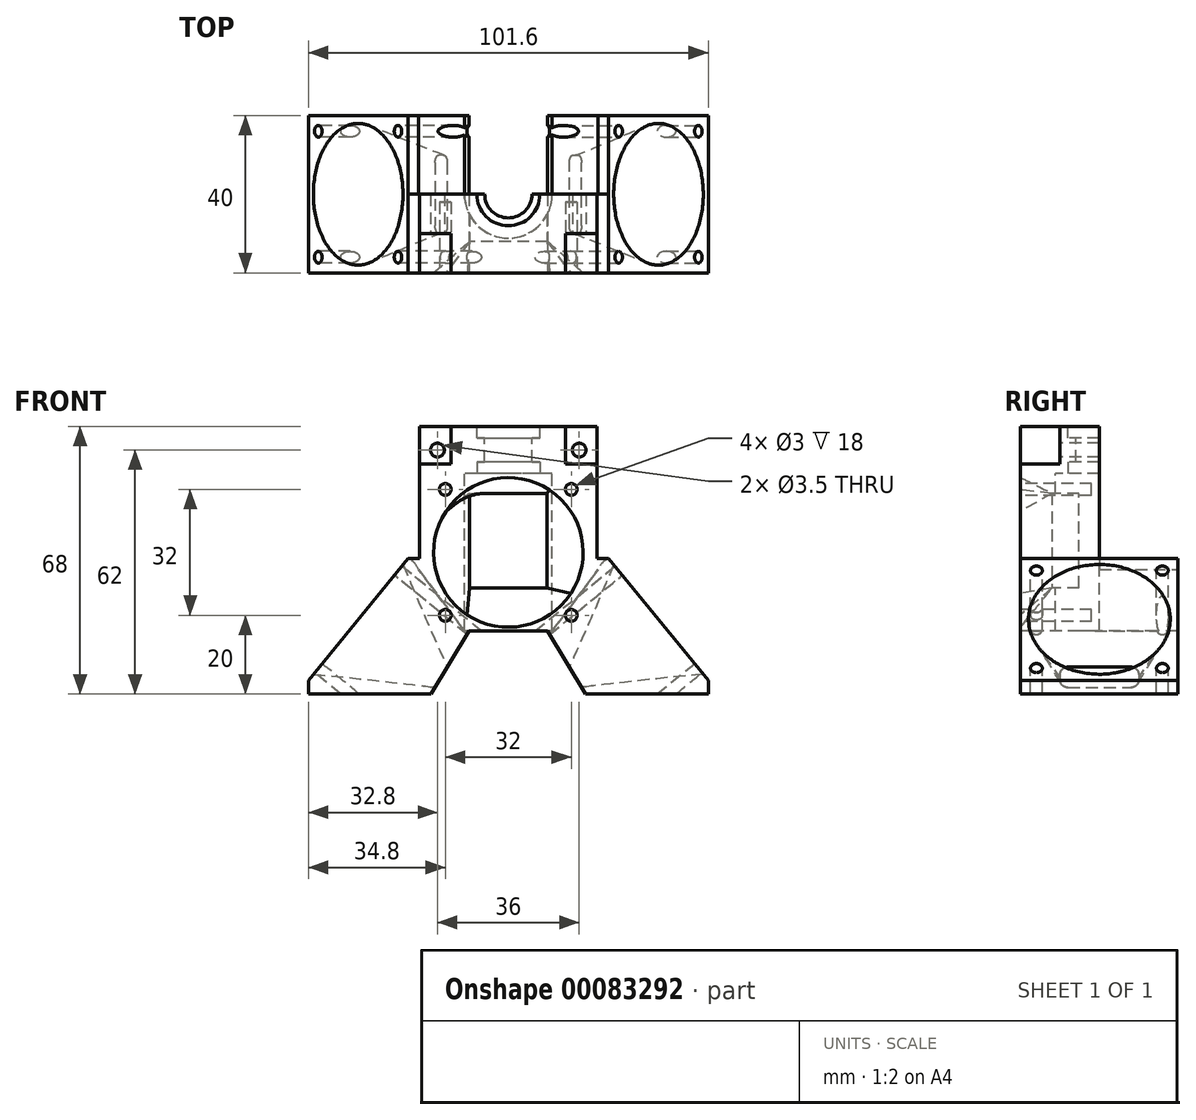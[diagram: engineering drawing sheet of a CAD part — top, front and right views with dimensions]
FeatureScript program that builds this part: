
annotation { "Feature Type Name" : "Feature", "Feature Type Description" : "" }
export const myFeature = defineFeature(function(context is Context, id is Id, definition is map)
    precondition{}
    {
        {
            var Q0;
            Q0=qCreatedBy(makeId("Front.planeOp"),FACE);
            var sketch = newSketch(context, id + "F0", { "sketchPlane" : qUnion([Q0])});
            skLineSegment(sketch, "E0.bottom", {"start": v(22.5, 6) * mm, "end": v(-22.5, 6) * mm});
            skLineSegment(sketch, "E0.top", {"start": v(22.5, -6) * mm, "end": v(-22.5, -6) * mm});
            skLineSegment(sketch, "E0.left", {"start": v(22.5, 6) * mm, "end": v(22.5, -6) * mm});
            skLineSegment(sketch, "E0.right", {"start": v(-22.5, 6) * mm, "end": v(-22.5, -6) * mm});
            skPoint(sketch, "E0.middle", {"position": v(0, 0) * mm});
            skCircle(sketch, "E1", {"center": v(-18, 0) * mm, "radius": 1.75 * mm});
            skCircle(sketch, "E2", {"center": v(-18, 0) * mm, "radius": 3.5 * mm, "construction": true});
            skCircle(sketch, "E3", {"center": v(18, 0) * mm, "radius": 1.75 * mm});
            skCircle(sketch, "E4", {"center": v(18, 0) * mm, "radius": 3.5 * mm, "construction": true});
            skLineSegment(sketch, "E5.bottom", {"start": v(-22.5, 6) * mm, "end": v(-14.5, 6) * mm});
            skLineSegment(sketch, "E5.top", {"start": v(-22.5, -3.5) * mm, "end": v(-14.5, -3.5) * mm});
            skLineSegment(sketch, "E5.left", {"start": v(-22.5, 6) * mm, "end": v(-22.5, -3.5) * mm});
            skLineSegment(sketch, "E5.right", {"start": v(-14.5, 6) * mm, "end": v(-14.5, -3.5) * mm});
            skLineSegment(sketch, "E6.bottom", {"start": v(22.5, 6) * mm, "end": v(14.5, 6) * mm});
            skLineSegment(sketch, "E6.top", {"start": v(22.5, -3.5) * mm, "end": v(14.5, -3.5) * mm});
            skLineSegment(sketch, "E6.left", {"start": v(22.5, 6) * mm, "end": v(22.5, -3.5) * mm});
            skLineSegment(sketch, "E6.right", {"start": v(14.5, 6) * mm, "end": v(14.5, -3.5) * mm});
            skSolve(sketch);
        }
        {
            var Q0;
            Q0=qSketchRegion(id+"F0",true);
            var Q1;
            Q1=makeQuery(id+"F0.imprint","IMPRINT",FACE,{"disambiguationData":[TD([[makeQuery(id+"F0.imprint","IMPRINT",EDGE,{"derivedFrom":sQuery(id+"F0.wireOp",EDGE,"E1")}),-1.0]])]});
            var Q2;
            Q2=makeQuery(id+"F0.imprint","IMPRINT",FACE,{"disambiguationData":[TD([[makeQuery(id+"F0.imprint","IMPRINT",EDGE,{"derivedFrom":sQuery(id+"F0.wireOp",EDGE,"E3")}),-1.0]])]});
            extrude(context, id + "F1", {"entities" : qUnion([Q0, Q1, Q2]), "oppositeDirection" : true, "depth" : 20 * mm});
        }
        {
            var Q0;
            Q0=makeQuery(id+"F0.imprint","IMPRINT",FACE,{"disambiguationData":[TD([[makeQuery(id+"F0.imprint","IMPRINT",EDGE,{"derivedFrom":sQuery(id+"F0.wireOp",EDGE,"E1")}),-1.0]])]});
            var Q1;
            Q1=makeQuery(id+"F0.imprint","IMPRINT",FACE,{"disambiguationData":[TD([[makeQuery(id+"F0.imprint","IMPRINT",EDGE,{"derivedFrom":sQuery(id+"F0.wireOp",EDGE,"E3")}),-1.0]])]});
            extrude(context, id + "F2", {"entities" : qUnion([Q0, Q1]), "operationType" : NewBodyOperationType.REMOVE, "oppositeDirection" : true, "depth" : 10 * mm});
        }
        {
            var Q0;
            Q0=makeQuery(id+"F1.opExtrude","SWEPT_FACE",FACE,{"disambiguationData":[OSD([sQuery(id+"F0.wireOp",EDGE,"E0.bottom")])]});
            var sketch = newSketch(context, id + "F3", { "sketchPlane" : qUnion([Q0])});
            skCircle(sketch, "E7", {"center": v(0, 20) * mm, "radius": 6 * mm});
            skCircle(sketch, "E8", {"center": v(0, 20) * mm, "radius": 8 * mm});
            skSolve(sketch);
        }
        {
            var Q0;
            {var subQ0=sQuery(id+"F3.wireOp",EDGE,"E7");var subQ1=makeQuery(id+"F1.opExtrude","CAP_EDGE",EDGE,{"disambiguationData":[OSD([sQuery(id+"F0.wireOp",EDGE,"E0.bottom")])],"isStart":false});var subQ2=makeQuery(id+"F3.imprint","INTERSECT",VERTEX,{"disambiguationData":[OD(0.0)],"derivedFrom":[subQ1,subQ0]});Q0=makeQuery(id+"F3.imprint","IMPRINT",FACE,{"disambiguationData":[TD([[makeQuery(id+"F3.imprint","IMPRINT",EDGE,{"disambiguationData":[TD([[subQ2,-1.0]])],"derivedFrom":subQ0}),1.0]])]});}
            var Q1;
            {var subQ0=sQuery(id+"F3.wireOp",EDGE,"E7");var subQ1=makeQuery(id+"F1.opExtrude","CAP_EDGE",EDGE,{"disambiguationData":[OSD([sQuery(id+"F0.wireOp",EDGE,"E0.bottom")])],"isStart":false});var subQ2=makeQuery(id+"F3.imprint","INTERSECT",VERTEX,{"disambiguationData":[OD(0.0)],"derivedFrom":[subQ1,subQ0]});Q1=makeQuery(id+"F3.imprint","IMPRINT",FACE,{"disambiguationData":[TD([[makeQuery(id+"F3.imprint","IMPRINT",EDGE,{"disambiguationData":[TD([[subQ2,1.0]])],"derivedFrom":subQ0}),1.0]])]});}
            extrude(context, id + "F4", {"entities" : qUnion([Q0, Q1]), "operationType" : NewBodyOperationType.REMOVE, "endBound" : BoundingType.THROUGH_ALL, "oppositeDirection" : true, "depth" : 25 * mm});
        }
        {
            var Q0;
            Q0=qSketchRegion(id+"F3",true);
            extrude(context, id + "F5", {"entities" : qUnion([Q0]), "operationType" : NewBodyOperationType.REMOVE, "oppositeDirection" : true, "depth" : 3 * mm});
        }
        {
            var Q0;
            Q0=makeQuery(id+"F1.opExtrude","SWEPT_FACE",FACE,{"disambiguationData":[OSD([sQuery(id+"F0.wireOp",EDGE,"E0.top")])]});
            var sketch = newSketch(context, id + "F6", { "sketchPlane" : qUnion([Q0])});
            skCircle(sketch, "E9", {"center": v(0, -20) * mm, "radius": 8 * mm});
            skSolve(sketch);
        }
        {
            var Q0;
            Q0=qSketchRegion(id+"F6",true);
            extrude(context, id + "F7", {"entities" : qUnion([Q0]), "operationType" : NewBodyOperationType.REMOVE, "oppositeDirection" : true, "depth" : 3 * mm});
        }
        {
            var Q0;
            {var subQ0=sQuery(id+"F0.wireOp",EDGE,"E0.top");Q0=makeQuery(id+"F6.imprint","IMPRINT",FACE,{"disambiguationData":[TD([[makeQuery(id+"F6.imprint","IMPRINT",EDGE,{"derivedFrom":makeQuery(id+"F1.opExtrude","CAP_EDGE",EDGE,{"disambiguationData":[OSD([subQ0])],"isStart":true})}),1.0]])]});}
            var sketch = newSketch(context, id + "F8", { "sketchPlane" : qUnion([Q0])});
            skLineSegment(sketch, "E10.bottom", {"start": v(-22.5, 0) * mm, "end": v(22.5, 0) * mm});
            skLineSegment(sketch, "E10.top", {"start": v(-22.5, -20) * mm, "end": v(-11.15, -20) * mm});
            skLineSegment(sketch, "E10.left", {"start": v(-22.5, 0) * mm, "end": v(-22.5, -20) * mm});
            skLineSegment(sketch, "E10.right", {"start": v(22.5, 0) * mm, "end": v(22.5, -20) * mm});
            skArc(sketch, "E11", {"start": v(11.15, -20) * mm, "mid": v(0, -8.85) * mm, "end": v(-11.15, -20) * mm});
            skLineSegment(sketch, "E12.trimOffspring", {"start": v(11.15, -20) * mm, "end": v(22.5, -20) * mm});
            skSolve(sketch);
        }
        {
            var Q0;
            Q0=qSketchRegion(id+"F8",true);
            extrude(context, id + "F9", {"entities" : qUnion([Q0]), "operationType" : NewBodyOperationType.ADD, "depth" : 40 * mm});
        }
        {
            var Q0;
            Q0=makeQuery(id+"F9.boolean.opBoolean","MERGE",FACE,{"derivedFrom":[makeQuery(id+"F1.opExtrude","CAP_FACE",FACE,{"disambiguationData":[OSD([sQuery(id+"F0.wireOp",EDGE,"E0.bottom"),sQuery(id+"F0.wireOp",EDGE,"E0.top"),sQuery(id+"F0.wireOp",EDGE,"E0.left"),sQuery(id+"F0.wireOp",EDGE,"E0.right"),sQuery(id+"F0.wireOp",EDGE,"E1"),sQuery(id+"F0.wireOp",EDGE,"E3")])],"isStart":true}),makeQuery(id+"F9.opExtrude","SWEPT_FACE",FACE,{"disambiguationData":[OSD([sQuery(id+"F8.wireOp",EDGE,"E10.bottom")])]})]});
            cPlane(context, id + "F10", {"entities" : qUnion([Q0]), "cplaneType" : CPlaneType.OFFSET, "offset" : 8 * mm, "oppositeDirection" : true, "width" : 150 * mm, "height" : 150 * mm});
        }
        {
            var Q0;
            Q0=qCreatedBy(id+"F10.planeOp",FACE);
            var sketch = newSketch(context, id + "F11", { "sketchPlane" : qUnion([Q0])});
            skLineSegment(sketch, "E13.bottom", {"start": v(9.89, -11) * mm, "end": v(-9.89, -11) * mm});
            skLineSegment(sketch, "E13.top", {"start": v(9.89, -35) * mm, "end": v(-9.89, -35) * mm});
            skLineSegment(sketch, "E13.left", {"start": v(9.89, -11) * mm, "end": v(9.89, -35) * mm});
            skLineSegment(sketch, "E13.right", {"start": v(-9.89, -11) * mm, "end": v(-9.89, -35) * mm});
            skPoint(sketch, "E13.middle", {"position": v(0, -23) * mm});
            skSolve(sketch);
        }
        {
            var Q0;
            Q0=makeQuery(id+"F9.boolean.opBoolean","MERGE",FACE,{"derivedFrom":[makeQuery(id+"F1.opExtrude","CAP_FACE",FACE,{"disambiguationData":[OSD([sQuery(id+"F0.wireOp",EDGE,"E0.bottom"),sQuery(id+"F0.wireOp",EDGE,"E0.top"),sQuery(id+"F0.wireOp",EDGE,"E0.left"),sQuery(id+"F0.wireOp",EDGE,"E0.right"),sQuery(id+"F0.wireOp",EDGE,"E1"),sQuery(id+"F0.wireOp",EDGE,"E3")])],"isStart":true}),makeQuery(id+"F9.opExtrude","SWEPT_FACE",FACE,{"disambiguationData":[OSD([sQuery(id+"F8.wireOp",EDGE,"E10.bottom")])]})]});
            var sketch = newSketch(context, id + "F12", { "sketchPlane" : qUnion([Q0])});
            skCircle(sketch, "E14", {"center": v(0, -26) * mm, "radius": 19 * mm});
            skSolve(sketch);
        }
        {
            var Q1;
            Q1=qSketchRegion(id+"F11",true);
            var Q2;
            Q2=qSketchRegion(id+"F12",true);
            loft(context, id + "F13", {"operationType" : NewBodyOperationType.REMOVE, "sheetProfilesArray" : [{ "sheetProfileEntities" : qUnion([Q1]) }, { "sheetProfileEntities" : qUnion([Q2]) }]});
        }
        {
            var Q0;
            Q0=qSketchRegion(id+"F11",true);
            extrude(context, id + "F14", {"entities" : qUnion([Q0]), "operationType" : NewBodyOperationType.REMOVE, "endBound" : BoundingType.THROUGH_ALL, "oppositeDirection" : true, "depth" : 25 * mm});
        }
        {
            var Q0;
            Q0=makeQuery(id+"F9.boolean.opBoolean","MERGE",FACE,{"derivedFrom":[makeQuery(id+"F1.opExtrude","CAP_FACE",FACE,{"disambiguationData":[OSD([sQuery(id+"F0.wireOp",EDGE,"E0.bottom"),sQuery(id+"F0.wireOp",EDGE,"E0.top"),sQuery(id+"F0.wireOp",EDGE,"E0.left"),sQuery(id+"F0.wireOp",EDGE,"E0.right"),sQuery(id+"F0.wireOp",EDGE,"E1"),sQuery(id+"F0.wireOp",EDGE,"E3")])],"isStart":true}),makeQuery(id+"F9.opExtrude","SWEPT_FACE",FACE,{"disambiguationData":[OSD([sQuery(id+"F8.wireOp",EDGE,"E10.bottom")])]})]});
            var sketch = newSketch(context, id + "F15", { "sketchPlane" : qUnion([Q0])});
            skLineSegment(sketch, "E15.bottom", {"start": v(16, -10) * mm, "end": v(-16, -10) * mm, "construction": true});
            skLineSegment(sketch, "E15.top", {"start": v(16, -42) * mm, "end": v(-16, -42) * mm, "construction": true});
            skLineSegment(sketch, "E15.left", {"start": v(16, -10) * mm, "end": v(16, -42) * mm, "construction": true});
            skLineSegment(sketch, "E15.right", {"start": v(-16, -10) * mm, "end": v(-16, -42) * mm, "construction": true});
            skPoint(sketch, "E15.middle", {"position": v(0, -26) * mm});
            skCircle(sketch, "E16", {"center": v(16, -10) * mm, "radius": 1.5 * mm});
            skCircle(sketch, "E17", {"center": v(-16, -10) * mm, "radius": 1.5 * mm});
            skCircle(sketch, "E18", {"center": v(-16, -42) * mm, "radius": 1.5 * mm});
            skCircle(sketch, "E19", {"center": v(16, -42) * mm, "radius": 1.5 * mm});
            skSolve(sketch);
        }
        {
            var Q0;
            Q0=qSketchRegion(id+"F15",true);
            extrude(context, id + "F16", {"entities" : qUnion([Q0]), "operationType" : NewBodyOperationType.REMOVE, "oppositeDirection" : true, "depth" : 18 * mm});
        }
        {
            var Q0;
            Q0=qCreatedBy(makeId("Front.planeOp"),FACE);
            var sketch = newSketch(context, id + "F17", { "sketchPlane" : qUnion([Q0])});
            skPoint(sketch, "E20", {"position": v(0, -68) * mm});
            skLineSegment(sketch, "E21", {"start": v(0, -68) * mm, "end": v(-20, -55.95) * mm, "construction": true});
            skLineSegment(sketch, "E22", {"start": v(-50.8, -58.5) * mm, "end": v(-50.8, -62) * mm});
            skLineSegment(sketch, "E23", {"start": v(-50.8, -62) * mm, "end": v(-19.64, -62) * mm});
            skLineSegment(sketch, "E24", {"start": v(-19.64, -62) * mm, "end": v(-10, -46) * mm});
            skLineSegment(sketch, "E25", {"start": v(-22.5, -27.52) * mm, "end": v(-25.5, -27.52) * mm});
            skLineSegment(sketch, "E26", {"start": v(-25.5, -27.52) * mm, "end": v(-50.8, -58.5) * mm});
            skPoint(sketch, "E27", {"position": v(-10, -61.97) * mm});
            skLineSegment(sketch, "E28", {"start": v(-22.5, -46) * mm, "end": v(-22.5, -27.52) * mm});
            skLineSegment(sketch, "E29", {"start": v(-10, -46) * mm, "end": v(-22.5, -46) * mm});
            skLineSegment(sketch, "E30", {"start": v(0, 42.58) * mm, "end": v(0, -74.7) * mm, "construction": true});
            skLineSegment(sketch, "E31.MirrorCS", {"start": v(50.8, -58.5) * mm, "end": v(50.8, -62) * mm});
            skLineSegment(sketch, "E32.MirrorCS", {"start": v(22.5, -27.52) * mm, "end": v(25.5, -27.52) * mm});
            skLineSegment(sketch, "E33.MirrorCS", {"start": v(0, -68) * mm, "end": v(20, -55.95) * mm, "construction": true});
            skLineSegment(sketch, "E34.MirrorCS", {"start": v(19.64, -62) * mm, "end": v(10, -46) * mm});
            skPoint(sketch, "E35.MirrorP", {"position": v(10, -61.97) * mm});
            skLineSegment(sketch, "E36.MirrorCS", {"start": v(50.8, -62) * mm, "end": v(19.64, -62) * mm});
            skLineSegment(sketch, "E37.MirrorCS", {"start": v(10, -46) * mm, "end": v(22.5, -46) * mm});
            skLineSegment(sketch, "E38.MirrorCS", {"start": v(22.5, -46) * mm, "end": v(22.5, -27.52) * mm});
            skLineSegment(sketch, "E39.MirrorCS", {"start": v(25.5, -27.52) * mm, "end": v(50.8, -58.5) * mm});
            skSolve(sketch);
        }
        {
            var Q0;
            Q0=makeQuery(id+"F17.imprint","IMPRINT",FACE,{"disambiguationData":[TD([[makeQuery(id+"F17.imprint","IMPRINT",EDGE,{"derivedFrom":sQuery(id+"F17.wireOp",EDGE,"f7ET7okq-i3aG-xWv0-ujYL-7c9q7adUJRvd")}),1.0]])]});
            var Q1;
            Q1=makeQuery(id+"F17.imprint","IMPRINT",FACE,{"disambiguationData":[TD([[makeQuery(id+"F17.imprint","IMPRINT",EDGE,{"derivedFrom":sQuery(id+"F17.wireOp",EDGE,"E22")}),1.0]])]});
            var Q2;
            Q2=makeQuery(id+"F17.imprint","IMPRINT",FACE,{"disambiguationData":[TD([[makeQuery(id+"F17.imprint","IMPRINT",EDGE,{"derivedFrom":sQuery(id+"F17.wireOp",EDGE,"E31.MirrorCS")}),-1.0]])]});
            extrude(context, id + "F18", {"entities" : qUnion([Q0, Q1, Q2]), "operationType" : NewBodyOperationType.ADD, "oppositeDirection" : true, "depth" : 40 * mm});
        }
        {
            var Q0;
            Q0=makeQuery(id+"F18.opExtrude","SWEPT_FACE",FACE,{"disambiguationData":[OSD([sQuery(id+"F17.wireOp",EDGE,"E26")])]});
            var sketch = newSketch(context, id + "F19", { "sketchPlane" : qUnion([Q0])});
            skCircle(sketch, "E40", {"center": v(-20, -57.45) * mm, "radius": 18 * mm});
            skSolve(sketch);
        }
        {
            var Q0;
            Q0=makeQuery(id+"F18.opExtrude","SWEPT_FACE",FACE,{"disambiguationData":[OSD([sQuery(id+"F17.wireOp",EDGE,"E24")])]});
            var sketch = newSketch(context, id + "F20", { "sketchPlane" : qUnion([Q0])});
            skLineSegment(sketch, "E41.bottom", {"start": v(28, -55.24) * mm, "end": v(12, -55.24) * mm});
            skLineSegment(sketch, "E41.top", {"start": v(28, -61.24) * mm, "end": v(12, -61.24) * mm});
            skLineSegment(sketch, "E41.left", {"start": v(30, -57.24) * mm, "end": v(30, -59.24) * mm});
            skLineSegment(sketch, "E41.right", {"start": v(10, -57.24) * mm, "end": v(10, -59.24) * mm});
            skPoint(sketch, "E41.middle", {"position": v(20, -58.24) * mm});
            skPoint(sketch, "E42.visualSharp", {"position": v(10, -55.24) * mm});
            skArc(sketch, "E42.filletArc", {"start": v(12, -55.24) * mm, "mid": v(10.59, -55.83) * mm, "end": v(10, -57.24) * mm});
            skPoint(sketch, "E43.visualSharp", {"position": v(10, -61.24) * mm});
            skArc(sketch, "E43.filletArc", {"start": v(10, -59.24) * mm, "mid": v(10.59, -60.66) * mm, "end": v(12, -61.24) * mm});
            skPoint(sketch, "E44.visualSharp", {"position": v(30, -61.24) * mm});
            skArc(sketch, "E44.filletArc", {"start": v(28, -61.24) * mm, "mid": v(29.41, -60.66) * mm, "end": v(30, -59.24) * mm});
            skPoint(sketch, "E45.visualSharp", {"position": v(30, -55.24) * mm});
            skArc(sketch, "E45.filletArc", {"start": v(30, -57.24) * mm, "mid": v(29.41, -55.83) * mm, "end": v(28, -55.24) * mm});
            skSolve(sketch);
        }
        {
            var Q1;
            Q1=makeQuery(id+"F19.imprint","IMPRINT",FACE,{"disambiguationData":[TD([[makeQuery(id+"F19.imprint","IMPRINT",EDGE,{"derivedFrom":sQuery(id+"F19.wireOp",EDGE,"E40")}),1.0]])]});
            var Q2;
            Q2=makeQuery(id+"F20.imprint","IMPRINT",FACE,{"disambiguationData":[TD([[makeQuery(id+"F20.imprint","IMPRINT",EDGE,{"derivedFrom":sQuery(id+"F20.wireOp",EDGE,"E41.bottom")}),1.0]])]});
            loft(context, id + "F21", {"operationType" : NewBodyOperationType.REMOVE, "sheetProfilesArray" : [{ "sheetProfileEntities" : qUnion([Q1]) }, { "sheetProfileEntities" : qUnion([Q2]) }]});
        }
        {
            var Q0;
            Q0=makeQuery(id+"F18.opExtrude","SWEPT_FACE",FACE,{"disambiguationData":[OSD([sQuery(id+"F17.wireOp",EDGE,"E39.MirrorCS")])]});
            var sketch = newSketch(context, id + "F22", { "sketchPlane" : qUnion([Q0])});
            skCircle(sketch, "E46", {"center": v(20, -57.45) * mm, "radius": 18 * mm});
            skSolve(sketch);
        }
        {
            var Q0;
            Q0=makeQuery(id+"F18.opExtrude","SWEPT_FACE",FACE,{"disambiguationData":[OSD([sQuery(id+"F17.wireOp",EDGE,"E34.MirrorCS")])]});
            var sketch = newSketch(context, id + "F23", { "sketchPlane" : qUnion([Q0])});
            skLineSegment(sketch, "E47.bottom", {"start": v(-12, -55.24) * mm, "end": v(-28, -55.24) * mm});
            skLineSegment(sketch, "E47.top", {"start": v(-12, -61.24) * mm, "end": v(-28, -61.24) * mm});
            skLineSegment(sketch, "E47.left", {"start": v(-10, -57.24) * mm, "end": v(-10, -59.24) * mm});
            skLineSegment(sketch, "E47.right", {"start": v(-30, -57.24) * mm, "end": v(-30, -59.24) * mm});
            skPoint(sketch, "E47.middle", {"position": v(-20, -58.24) * mm});
            skPoint(sketch, "E48.visualSharp", {"position": v(-30, -55.24) * mm});
            skArc(sketch, "E48.filletArc", {"start": v(-28, -55.24) * mm, "mid": v(-29.41, -55.83) * mm, "end": v(-30, -57.24) * mm});
            skPoint(sketch, "E49.visualSharp", {"position": v(-10, -55.24) * mm});
            skArc(sketch, "E49.filletArc", {"start": v(-10, -57.24) * mm, "mid": v(-10.59, -55.83) * mm, "end": v(-12, -55.24) * mm});
            skPoint(sketch, "E50.visualSharp", {"position": v(-10, -61.24) * mm});
            skArc(sketch, "E50.filletArc", {"start": v(-12, -61.24) * mm, "mid": v(-10.59, -60.66) * mm, "end": v(-10, -59.24) * mm});
            skPoint(sketch, "E51.visualSharp", {"position": v(-30, -61.24) * mm});
            skArc(sketch, "E51.filletArc", {"start": v(-30, -59.24) * mm, "mid": v(-29.41, -60.66) * mm, "end": v(-28, -61.24) * mm});
            skSolve(sketch);
        }
        {
            var Q1;
            Q1=makeQuery(id+"F22.imprint","IMPRINT",FACE,{"disambiguationData":[TD([[makeQuery(id+"F22.imprint","IMPRINT",EDGE,{"derivedFrom":sQuery(id+"F22.wireOp",EDGE,"E46")}),1.0]])]});
            var Q2;
            Q2=makeQuery(id+"F23.imprint","IMPRINT",FACE,{"disambiguationData":[TD([[makeQuery(id+"F23.imprint","IMPRINT",EDGE,{"derivedFrom":sQuery(id+"F23.wireOp",EDGE,"E47.bottom")}),1.0]])]});
            loft(context, id + "F24", {"operationType" : NewBodyOperationType.REMOVE, "sheetProfilesArray" : [{ "sheetProfileEntities" : qUnion([Q1]) }, { "sheetProfileEntities" : qUnion([Q2]) }]});
        }
        {
            var Q0;
            {var subQ0=sQuery(id+"F17.wireOp",EDGE,"E25");Q0=makeQuery(id+"F18.boolean.opBoolean","SPLIT",EDGE,{"disambiguationData":[topologyDisambiguationEdgeConnected([makeQuery(id+"F1.opExtrude","SWEPT_FACE",FACE,{"disambiguationData":[OSD([sQuery(id+"F0.wireOp",EDGE,"E0.right")])]})])],"derivedFrom":makeQuery(id+"F18.opExtrude","SWEPT_EDGE",EDGE,{"disambiguationData":[OSD([subQ0,sQuery(id+"F17.wireOp",EDGE,"E28")])]})});}
            var Q1;
            {var subQ0=sQuery(id+"F17.wireOp",EDGE,"E32.MirrorCS");Q1=makeQuery(id+"F18.boolean.opBoolean","SPLIT",EDGE,{"disambiguationData":[topologyDisambiguationEdgeConnected([makeQuery(id+"F1.opExtrude","SWEPT_FACE",FACE,{"disambiguationData":[OSD([sQuery(id+"F0.wireOp",EDGE,"E0.left")])]})])],"derivedFrom":makeQuery(id+"F18.opExtrude","SWEPT_EDGE",EDGE,{"disambiguationData":[OSD([subQ0,sQuery(id+"F17.wireOp",EDGE,"E38.MirrorCS")])]})});}
            fillet(context, id + "F25", {"entities" : qUnion([Q0, Q1]), "radius" : 5 * mm, "tangentPropagation" : true, "allowEdgeOverflow" : false});
        }
        {
            var Q0;
            Q0=makeQuery(id+"F19.imprint","IMPRINT",FACE,{"disambiguationData":[TD([[makeQuery(id+"F19.imprint","IMPRINT",EDGE,{"derivedFrom":sQuery(id+"F19.wireOp",EDGE,"E40")}),-1.0]])]});
            var sketch = newSketch(context, id + "F26", { "sketchPlane" : qUnion([Q0])});
            skLineSegment(sketch, "E52.bottom", {"start": v(-4, -73.45) * mm, "end": v(-36, -73.45) * mm, "construction": true});
            skLineSegment(sketch, "E52.top", {"start": v(-4, -41.45) * mm, "end": v(-36, -41.45) * mm, "construction": true});
            skLineSegment(sketch, "E52.left", {"start": v(-4, -73.45) * mm, "end": v(-4, -41.45) * mm, "construction": true});
            skLineSegment(sketch, "E52.right", {"start": v(-36, -73.45) * mm, "end": v(-36, -41.45) * mm, "construction": true});
            skPoint(sketch, "E52.middle", {"position": v(-20, -57.45) * mm});
            skCircle(sketch, "E53", {"center": v(-36, -73.45) * mm, "radius": 1.5 * mm});
            skCircle(sketch, "E54", {"center": v(-4, -73.45) * mm, "radius": 1.5 * mm});
            skCircle(sketch, "E55", {"center": v(-4, -41.45) * mm, "radius": 1.5 * mm});
            skCircle(sketch, "E56", {"center": v(-36, -41.45) * mm, "radius": 1.5 * mm});
            skSolve(sketch);
        }
        {
            var Q0;
            Q0=qSketchRegion(id+"F26",true);
            extrude(context, id + "F27", {"entities" : qUnion([Q0]), "operationType" : NewBodyOperationType.REMOVE, "endBound" : BoundingType.THROUGH_ALL, "oppositeDirection" : true, "depth" : 25 * mm});
        }
        {
            var Q0;
            Q0=makeQuery(id+"F18.opExtrude","SWEPT_FACE",FACE,{"disambiguationData":[OSD([sQuery(id+"F17.wireOp",EDGE,"E39.MirrorCS")])]});
            var sketch = newSketch(context, id + "F28", { "sketchPlane" : qUnion([Q0])});
            skLineSegment(sketch, "E57.bottom", {"start": v(36, -73.45) * mm, "end": v(4, -73.45) * mm, "construction": true});
            skLineSegment(sketch, "E57.top", {"start": v(36, -41.45) * mm, "end": v(4, -41.45) * mm, "construction": true});
            skLineSegment(sketch, "E57.left", {"start": v(36, -73.45) * mm, "end": v(36, -41.45) * mm, "construction": true});
            skLineSegment(sketch, "E57.right", {"start": v(4, -73.45) * mm, "end": v(4, -41.45) * mm, "construction": true});
            skPoint(sketch, "E57.middle", {"position": v(20, -57.45) * mm});
            skCircle(sketch, "E58", {"center": v(4, -73.45) * mm, "radius": 1.5 * mm});
            skCircle(sketch, "E59", {"center": v(36, -73.45) * mm, "radius": 1.5 * mm});
            skCircle(sketch, "E60", {"center": v(36, -41.45) * mm, "radius": 1.5 * mm});
            skCircle(sketch, "E61", {"center": v(4, -41.45) * mm, "radius": 1.5 * mm});
            skSolve(sketch);
        }
        {
            var Q0;
            Q0=qSketchRegion(id+"F28",true);
            extrude(context, id + "F29", {"entities" : qUnion([Q0]), "operationType" : NewBodyOperationType.REMOVE, "endBound" : BoundingType.THROUGH_ALL, "oppositeDirection" : true, "depth" : 25 * mm});
        }
        {
            var Q0;
            Q0=makeQuery(id+"F18.opExtrude","SWEPT_EDGE",EDGE,{"disambiguationData":[OSD([sQuery(id+"F17.wireOp",EDGE,"E37.MirrorCS"),sQuery(id+"F17.wireOp",EDGE,"E38.MirrorCS")])]});
            chamfer(context, id + "F30", {"entities" : qUnion([Q0]), "chamferType" : ChamferType.TWO_OFFSETS, "width1" : 20 * mm, "oppositeDirection" : false, "width2" : 12.5 * mm, "tangentPropagation" : true});
        }
        {
            var Q0;
            Q0=makeQuery(id+"F18.opExtrude","SWEPT_EDGE",EDGE,{"disambiguationData":[OSD([sQuery(id+"F17.wireOp",EDGE,"E28"),sQuery(id+"F17.wireOp",EDGE,"E29")])]});
            chamfer(context, id + "F31", {"entities" : qUnion([Q0]), "chamferType" : ChamferType.TWO_OFFSETS, "width1" : 12.5 * mm, "oppositeDirection" : false, "width2" : 20 * mm, "tangentPropagation" : true});
        }
    });
